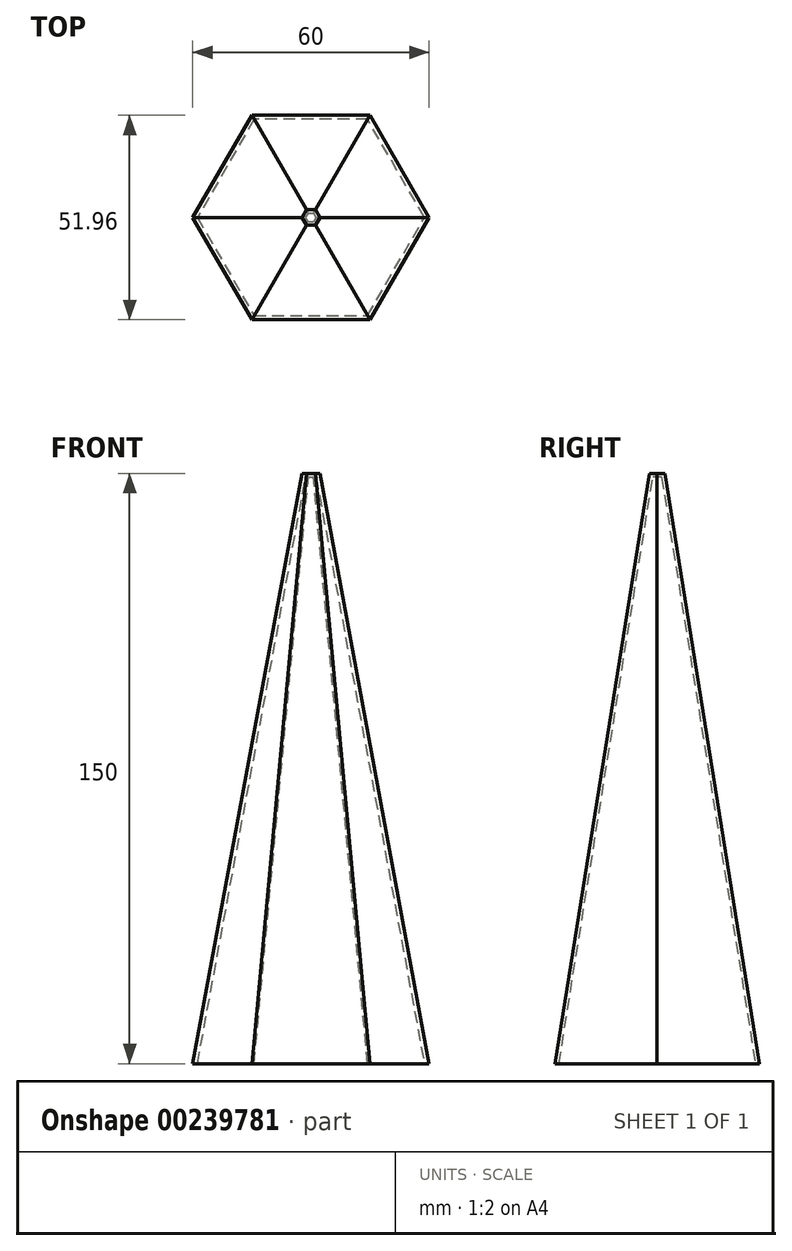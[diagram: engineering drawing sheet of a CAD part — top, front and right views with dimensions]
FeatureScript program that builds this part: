
annotation { "Feature Type Name" : "Feature", "Feature Type Description" : "" }
export const myFeature = defineFeature(function(context is Context, id is Id, definition is map)
    precondition{}
    {
        {
            var Q0;
            Q0=qCreatedBy(makeId("Top.planeOp"),FACE);
            var sketch = newSketch(context, id + "F0", { "sketchPlane" : qUnion([Q0])});
            skCircle(sketch, "E0.cCircle", {"center": v(0, 0) * mm, "radius": 30 * mm, "construction": true});
            skLineSegment(sketch, "E0.0", {"start": v(30, 0) * mm, "end": v(15, -25.98) * mm});
            skLineSegment(sketch, "E0.1", {"start": v(15, -25.98) * mm, "end": v(-15, -25.98) * mm});
            skLineSegment(sketch, "E0.2", {"start": v(-15, -25.98) * mm, "end": v(-30, 0) * mm});
            skLineSegment(sketch, "E0.3", {"start": v(-30, 0) * mm, "end": v(-15, 25.98) * mm});
            skLineSegment(sketch, "E0.4", {"start": v(-15, 25.98) * mm, "end": v(15, 25.98) * mm});
            skLineSegment(sketch, "E0.5", {"start": v(15, 25.98) * mm, "end": v(30, 0) * mm});
            skSolve(sketch);
        }
        {
            var Q0;
            Q0=makeQuery(id+"F0.imprint","IMPRINT",FACE,{"disambiguationData":[TD([[makeQuery(id+"F0.imprint","IMPRINT",EDGE,{"derivedFrom":sQuery(id+"F0.wireOp",EDGE,"E0.0")}),-1.0]])]});
            extrude(context, id + "F1", {"entities" : qUnion([Q0]), "depth" : 150 * mm});
        }
        {
            var Q0;
            Q0=makeQuery(id+"F1.opExtrude","CAP_EDGE",EDGE,{"disambiguationData":[OSD([sQuery(id+"F0.wireOp",EDGE,"E0.2")])],"isStart":false});
            var Q1;
            Q1=makeQuery(id+"F1.opExtrude","CAP_EDGE",EDGE,{"disambiguationData":[OSD([sQuery(id+"F0.wireOp",EDGE,"E0.1")])],"isStart":false});
            var Q2;
            Q2=makeQuery(id+"F1.opExtrude","CAP_EDGE",EDGE,{"disambiguationData":[OSD([sQuery(id+"F0.wireOp",EDGE,"E0.0")])],"isStart":false});
            var Q3;
            Q3=makeQuery(id+"F1.opExtrude","CAP_EDGE",EDGE,{"disambiguationData":[OSD([sQuery(id+"F0.wireOp",EDGE,"E0.5")])],"isStart":false});
            var Q4;
            Q4=makeQuery(id+"F1.opExtrude","CAP_EDGE",EDGE,{"disambiguationData":[OSD([sQuery(id+"F0.wireOp",EDGE,"E0.4")])],"isStart":false});
            var Q5;
            Q5=makeQuery(id+"F1.opExtrude","CAP_FACE",FACE,{"disambiguationData":[OSD([sQuery(id+"F0.wireOp",EDGE,"E0.0"),sQuery(id+"F0.wireOp",EDGE,"E0.1"),sQuery(id+"F0.wireOp",EDGE,"E0.2"),sQuery(id+"F0.wireOp",EDGE,"E0.3"),sQuery(id+"F0.wireOp",EDGE,"E0.4"),sQuery(id+"F0.wireOp",EDGE,"E0.5")])],"isStart":false});
            chamfer(context, id + "F2", {"entities" : qUnion([Q0, Q1, Q2, Q3, Q4, Q5]), "chamferType" : ChamferType.TWO_OFFSETS, "width1" : 150 * mm, "oppositeDirection" : false, "width2" : 24 * mm, "tangentPropagation" : true});
        }
        {
            var Q0;
            Q0=makeQuery(id+"F1.opExtrude","CAP_FACE",FACE,{"disambiguationData":[OSD([sQuery(id+"F0.wireOp",EDGE,"E0.0"),sQuery(id+"F0.wireOp",EDGE,"E0.1"),sQuery(id+"F0.wireOp",EDGE,"E0.2"),sQuery(id+"F0.wireOp",EDGE,"E0.3"),sQuery(id+"F0.wireOp",EDGE,"E0.4"),sQuery(id+"F0.wireOp",EDGE,"E0.5")])],"isStart":true});
            shell(context, id + "F3", {"entities" : qUnion([Q0]), "thickness" : 1 * mm});
        }
    });
